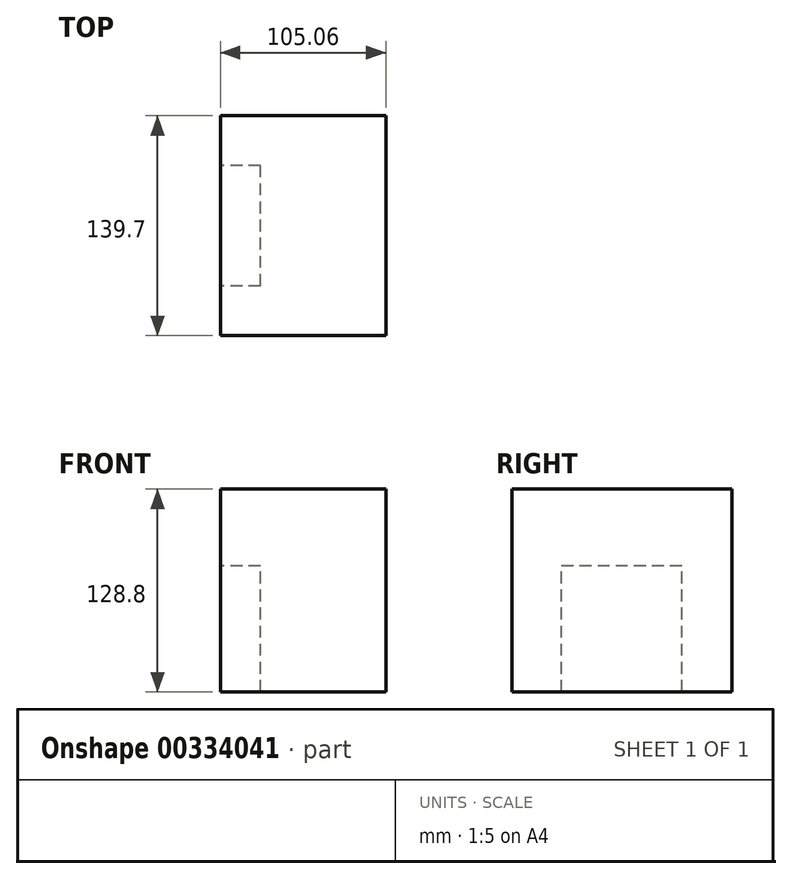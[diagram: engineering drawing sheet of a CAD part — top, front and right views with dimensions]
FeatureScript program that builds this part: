
annotation { "Feature Type Name" : "Feature", "Feature Type Description" : "" }
export const myFeature = defineFeature(function(context is Context, id is Id, definition is map)
    precondition{}
    {
        {
            var Q0;
            Q0=qCreatedBy(makeId("Front.planeOp"),FACE);
            var sketch = newSketch(context, id + "F0", { "sketchPlane" : qUnion([Q0])});
            skLineSegment(sketch, "E0.bottom", {"start": v(-52.53, 64.4) * mm, "end": v(52.53, 64.4) * mm});
            skLineSegment(sketch, "E0.top", {"start": v(-52.53, -64.4) * mm, "end": v(52.53, -64.4) * mm});
            skLineSegment(sketch, "E0.left", {"start": v(-52.53, 64.4) * mm, "end": v(-52.53, -64.4) * mm});
            skLineSegment(sketch, "E0.right", {"start": v(52.53, 64.4) * mm, "end": v(52.53, -64.4) * mm});
            skPoint(sketch, "E0.middle", {"position": v(0, 0) * mm});
            skSolve(sketch);
        }
        {
            var Q0;
            Q0 = qSketchRegion(id + "F0", true);
            var sketch = newSketch(context, id + "F1", { "sketchPlane" : qUnion([Q0])});
            skSolve(sketch);
        }
        {
            var Q0;
            Q0=makeQuery(id+"F0.imprint","IMPRINT",FACE,{"disambiguationData":[TD([[makeQuery(id+"F0.imprint","IMPRINT",EDGE,{"derivedFrom":sQuery(id+"F0.wireOp",EDGE,"E0.bottom")}),-1.0]])]});
            extrude(context, id + "F2", {"entities" : qUnion([Q0]), "endBound" : BoundingType.SYMMETRIC, "depth" : 127 * mm});
        }
        {
            var Q0;
            Q0=makeQuery(id+"F2.opExtrude","CAP_FACE",FACE,{"disambiguationData":[OSD([sQuery(id+"F0.wireOp",EDGE,"E0.bottom"),sQuery(id+"F0.wireOp",EDGE,"E0.top"),sQuery(id+"F0.wireOp",EDGE,"E0.left"),sQuery(id+"F0.wireOp",EDGE,"E0.right")])],"isStart":false});
            var sketch = newSketch(context, id + "F3", { "sketchPlane" : qUnion([Q0])});
            skLineSegment(sketch, "E1.bottom", {"start": v(0, -64.4) * mm, "end": v(-23.9, -64.4) * mm});
            skLineSegment(sketch, "E1.top", {"start": v(0, -33.22) * mm, "end": v(-23.9, -33.22) * mm, "construction": true});
            skLineSegment(sketch, "E1.left", {"start": v(0, -64.4) * mm, "end": v(0, -33.22) * mm});
            skLineSegment(sketch, "E1.right", {"start": v(-23.9, -64.4) * mm, "end": v(-23.9, -33.22) * mm});
            skSolve(sketch);
        }
        {
            var Q0;
            {var subQ2=sQuery(id+"F3.wireOp",EDGE,"E1.bottom");Q0=makeQuery(id+"F3.imprint","IMPRINT",FACE,{"disambiguationData":[TD([[makeQuery(id+"F3.imprint","IMPRINT",EDGE,{"derivedFrom":subQ2}),1.0]])]});}
            extrude(context, id + "F4", {"entities" : qUnion([Q0]), "operationType" : NewBodyOperationType.ADD, "depth" : 12.7 * mm});
        }
        {
            var Q0;
            {var subQ0=sQuery(id+"F0.wireOp",EDGE,"E0.left");Q0=makeQuery(id+"F4.boolean.opBoolean","MERGE",FACE,{"derivedFrom":[makeQuery(id+"F2.opExtrude","SWEPT_FACE",FACE,{"disambiguationData":[OSD([subQ0])]}),makeQuery(id+"F4.opExtrude","SWEPT_FACE",FACE,{"disambiguationData":[OSD([subQ0])]})]});}
            var sketch = newSketch(context, id + "F5", { "sketchPlane" : qUnion([Q0])});
            skLineSegment(sketch, "E2.bottom", {"start": v(-31.87, -64.4) * mm, "end": v(44.57, -64.4) * mm});
            skLineSegment(sketch, "E2.top", {"start": v(-31.87, 15.6) * mm, "end": v(44.57, 15.6) * mm});
            skLineSegment(sketch, "E2.left", {"start": v(-31.87, -64.4) * mm, "end": v(-31.87, 15.6) * mm});
            skLineSegment(sketch, "E2.right", {"start": v(44.57, -64.4) * mm, "end": v(44.57, 15.6) * mm});
            skPoint(sketch, "E2.middle", {"position": v(6.35, -24.4) * mm});
            skPoint(sketch, "E2.middle.positionSnap0", {"position": v(6.35, -64.4) * mm});
            skPoint(sketch, "E2.centerSnap0", {"position": v(6.35, -64.4) * mm});
            skSolve(sketch);
        }
        {
            var Q0;
            Q0=makeQuery(id+"F5.imprint","IMPRINT",FACE,{"disambiguationData":[TD([[makeQuery(id+"F5.imprint","IMPRINT",EDGE,{"derivedFrom":sQuery(id+"F5.wireOp",EDGE,"E2.bottom")}),-1.0]])]});
            extrude(context, id + "F6", {"entities" : qUnion([Q0]), "operationType" : NewBodyOperationType.REMOVE, "oppositeDirection" : true, "depth" : 25.4 * mm});
        }
    });
